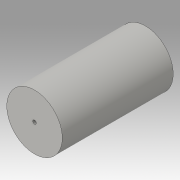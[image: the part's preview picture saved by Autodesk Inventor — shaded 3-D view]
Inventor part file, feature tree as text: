
AUTODESK INVENTOR PART (.ipt)
format: ipt  version: 2016 (Build 200138000, 138)  size: 81,920 bytes
history: native  units: in
note: dims shown in document units (in); Inventor stores cm internally (conversion verified against a paired STEP export)
features: extrude x1, hole x1, sketch x1
ambient origin geometry x8: Origin, YZ Plane, XZ Plane, XY Plane, X Axis, Y Axis, Z Axis, Center Point
bodies: Solid1 (feature_tree)
feature tree (3):
  extrude  "Extrusion1"  Depth=6.0in TaperAngle=0.0deg
  hole  "Hole1"  [1 undecoded]
  sketch  "Sketch1"  dims[d0=3.0in d1=6.0in d2=0.0in d3=1.0in d4=1.0in d5=0.188in d6=0.75in d7=0.375in d8=0.25in d9=0.5635in d10=1.0in d11=0.8108in]
note: 1 required parameter value undecoded (feature->parameter linkage not recoverable at this tier; creation-order binding heuristic only, values carry confidence <= 0.55)
